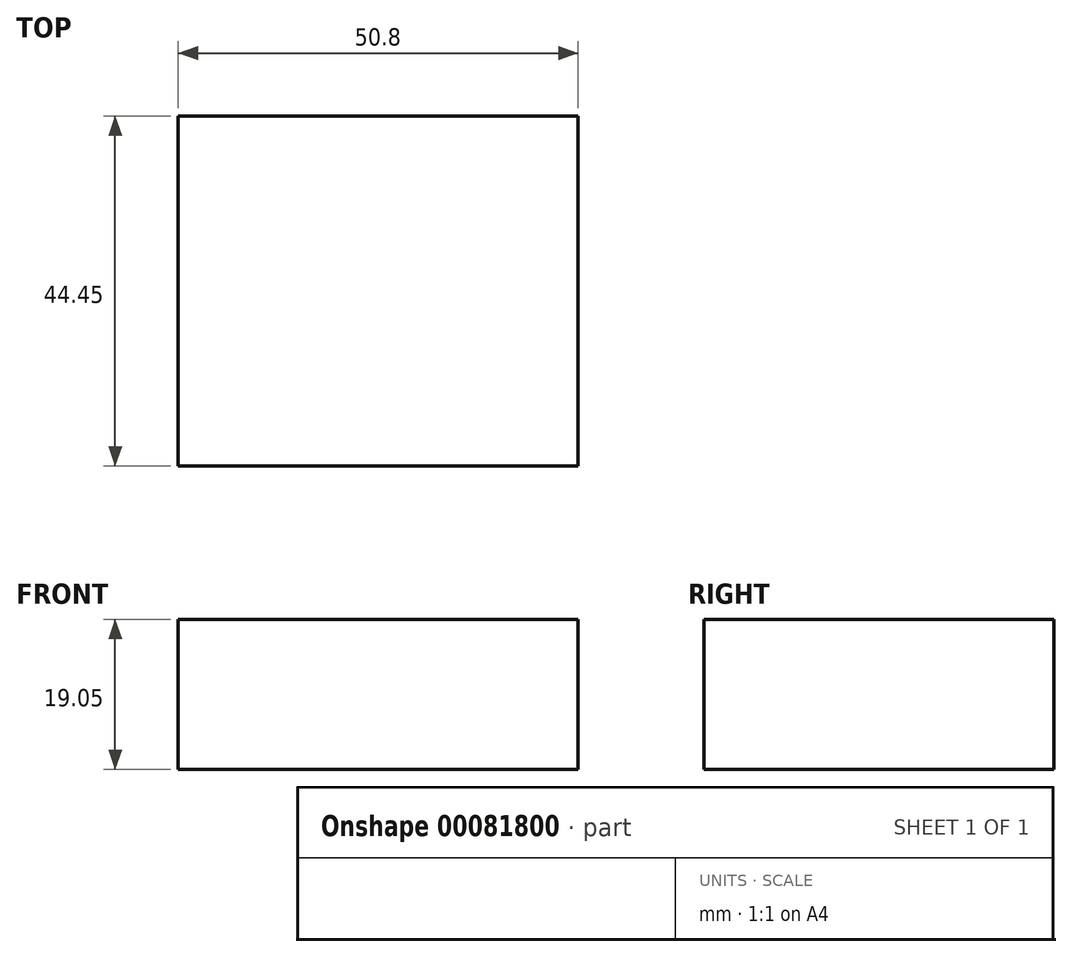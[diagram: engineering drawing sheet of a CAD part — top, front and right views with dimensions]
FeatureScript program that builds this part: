
annotation { "Feature Type Name" : "Feature", "Feature Type Description" : "" }
export const myFeature = defineFeature(function(context is Context, id is Id, definition is map)
    precondition{}
    {
        {
            var Q0;
            Q0=qCreatedBy(makeId("Top.planeOp"),FACE);
            var sketch = newSketch(context, id + "F0", { "sketchPlane" : qUnion([Q0])});
            skLineSegment(sketch, "E0.bottom", {"start": v(-17.97, 24.64) * mm, "end": v(32.83, 24.64) * mm});
            skLineSegment(sketch, "E0.top", {"start": v(-17.97, -19.81) * mm, "end": v(32.83, -19.81) * mm});
            skLineSegment(sketch, "E0.left", {"start": v(-17.97, 24.64) * mm, "end": v(-17.97, -19.81) * mm});
            skLineSegment(sketch, "E0.right", {"start": v(32.83, 24.64) * mm, "end": v(32.83, -19.81) * mm});
            skLineSegment(sketch, "E1.bottom", {"start": v(26.08, -18.78) * mm, "end": v(29.97, -18.78) * mm});
            skLineSegment(sketch, "E1.top", {"start": v(26.08, -18.78) * mm, "end": v(29.97, -18.78) * mm});
            skLineSegment(sketch, "E1.left", {"start": v(26.08, -18.78) * mm, "end": v(26.08, -18.78) * mm});
            skLineSegment(sketch, "E1.right", {"start": v(29.97, -18.78) * mm, "end": v(29.97, -18.78) * mm});
            skSolve(sketch);
        }
        {
            var Q0;
            Q0=makeQuery(id+"F0.imprint","IMPRINT",FACE,{"disambiguationData":[TD([[makeQuery(id+"F0.imprint","IMPRINT",EDGE,{"derivedFrom":sQuery(id+"F0.wireOp",EDGE,"E0.bottom")}),-1.0]])]});
            extrude(context, id + "F1", {"entities" : qUnion([Q0]), "depth" : 19.05 * mm});
        }
    });
